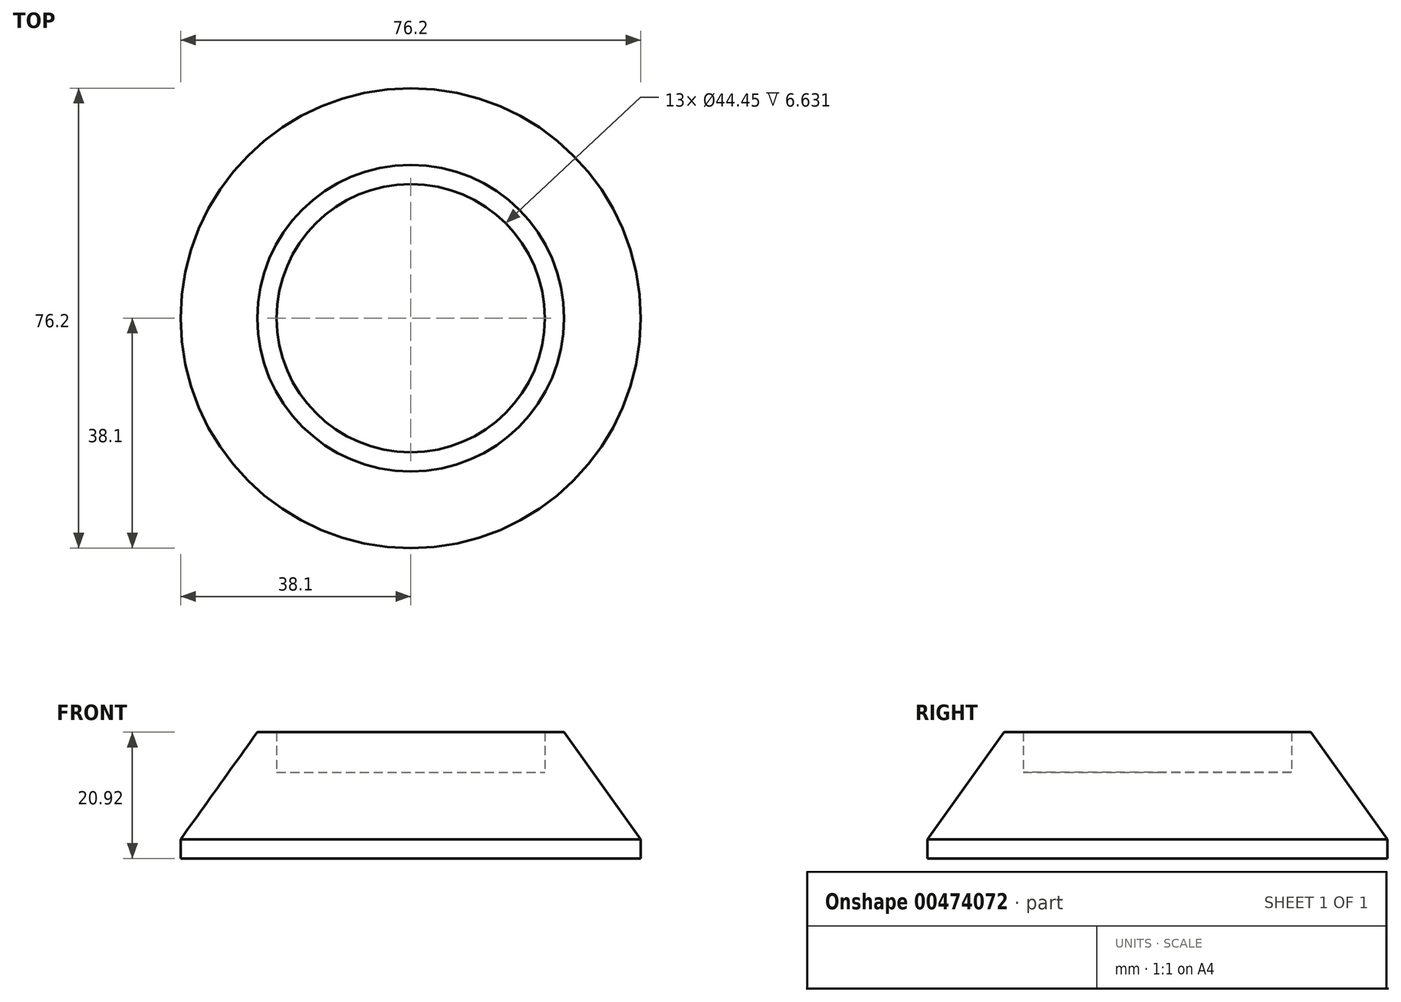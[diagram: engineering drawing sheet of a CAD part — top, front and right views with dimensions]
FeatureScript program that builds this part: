
annotation { "Feature Type Name" : "Feature", "Feature Type Description" : "" }
export const myFeature = defineFeature(function(context is Context, id is Id, definition is map)
    precondition{}
    {
        {
            var Q0;
            Q0=qCreatedBy(makeId("Top.planeOp"),FACE);
            var sketch = newSketch(context, id + "F0", { "sketchPlane" : qUnion([Q0])});
            skCircle(sketch, "E0", {"center": v(0, 0) * mm, "radius": 38.1 * mm});
            skCircle(sketch, "E1", {"center": v(0, 0) * mm, "radius": 22.23 * mm});
            skSolve(sketch);
        }
        {
            var Q0;
            Q0=qCreatedBy(makeId("Front.planeOp"),FACE);
            var sketch = newSketch(context, id + "F1", { "sketchPlane" : qUnion([Q0])});
            skLineSegment(sketch, "E2.0", {"start": v(-22.23, 0) * mm, "end": v(22.23, 0) * mm});
            skLineSegment(sketch, "E3.0", {"start": v(-38.1, 0) * mm, "end": v(38.1, 0) * mm});
            skLineSegment(sketch, "E4", {"start": v(0, 0) * mm, "end": v(22.23, 0) * mm});
            skLineSegment(sketch, "E5", {"start": v(22.23, 6.63) * mm, "end": v(22.23, 0) * mm});
            skLineSegment(sketch, "E6", {"start": v(38.1, -11.11) * mm, "end": v(38.1, -14.29) * mm});
            skLineSegment(sketch, "E7", {"start": v(0, -14.29) * mm, "end": v(38.1, -14.29) * mm});
            skLineSegment(sketch, "E8", {"start": v(0, -14.29) * mm, "end": v(0, 0) * mm});
            skLineSegment(sketch, "E9", {"start": v(22.23, 6.63) * mm, "end": v(25.4, 6.63) * mm});
            skLineSegment(sketch, "E10", {"start": v(25.4, 6.63) * mm, "end": v(38.1, -11.11) * mm});
            skSolve(sketch);
        }
        {
            var Q0;
            {var subQ0=sQuery(id+"F1.wireOp",EDGE,"E6");Q0=makeQuery(id+"F1.imprint","IMPRINT",FACE,{"disambiguationData":[TD([[makeQuery(id+"F1.imprint","IMPRINT",EDGE,{"derivedFrom":subQ0}),-1.0]])]});}
            var Q1;
            {var subQ3=sQuery(id+"F1.wireOp",EDGE,"E5");Q1=makeQuery(id+"F1.imprint","IMPRINT",FACE,{"disambiguationData":[TD([[makeQuery(id+"F1.imprint","IMPRINT",EDGE,{"derivedFrom":subQ3}),1.0]])]});}
            var Q2;
            Q2=sQuery(id+"F1.wireOp",EDGE,"E8");
            revolve(context, id + "F2", {"entities" : qUnion([Q0, Q1]), "axis" : qUnion([Q2]), "revolveType" : RevolveType.FULL});
        }
    });
